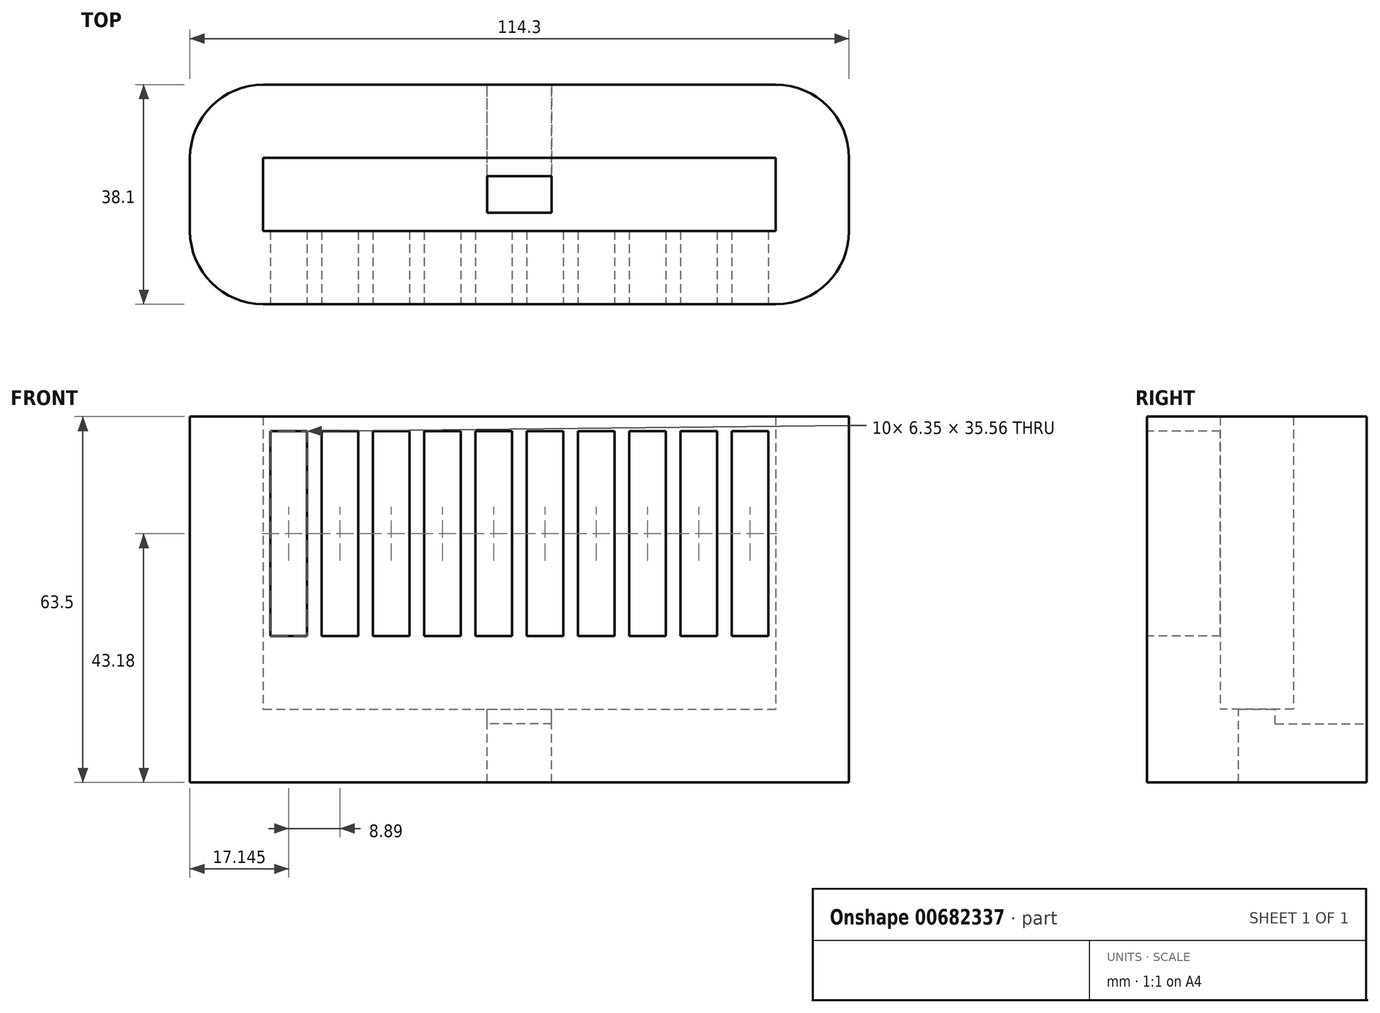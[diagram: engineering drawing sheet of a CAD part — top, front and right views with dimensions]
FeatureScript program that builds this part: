
annotation { "Feature Type Name" : "Feature", "Feature Type Description" : "" }
export const myFeature = defineFeature(function(context is Context, id is Id, definition is map)
    precondition{}
    {
        {
            var Q0;
            Q0=qCreatedBy(makeId("Top.planeOp"),FACE);
            var sketch = newSketch(context, id + "F0", { "sketchPlane" : qUnion([Q0])});
            skLineSegment(sketch, "E0.bottom", {"start": v(0, 0) * mm, "end": v(114.3, 0) * mm});
            skLineSegment(sketch, "E0.top", {"start": v(0, -38.1) * mm, "end": v(114.3, -38.1) * mm});
            skLineSegment(sketch, "E0.left", {"start": v(0, 0) * mm, "end": v(0, -38.1) * mm});
            skLineSegment(sketch, "E0.right", {"start": v(114.3, 0) * mm, "end": v(114.3, -38.1) * mm});
            skLineSegment(sketch, "E1.bottom", {"start": v(12.7, -12.7) * mm, "end": v(101.6, -12.7) * mm});
            skLineSegment(sketch, "E1.top", {"start": v(12.7, -25.4) * mm, "end": v(101.6, -25.4) * mm});
            skLineSegment(sketch, "E1.left", {"start": v(12.7, -12.7) * mm, "end": v(12.7, -25.4) * mm});
            skLineSegment(sketch, "E1.right", {"start": v(101.6, -12.7) * mm, "end": v(101.6, -25.4) * mm});
            skPoint(sketch, "E2", {"position": v(57.15, -12.7) * mm});
            skPoint(sketch, "E3", {"position": v(57.15, 0) * mm});
            skPoint(sketch, "E4", {"position": v(57.15, -38.1) * mm});
            skPoint(sketch, "E5", {"position": v(57.15, -25.4) * mm});
            skPoint(sketch, "E6", {"position": v(0, -19.05) * mm});
            skPoint(sketch, "E7", {"position": v(12.7, -19.05) * mm});
            skPoint(sketch, "E8", {"position": v(101.6, -19.05) * mm});
            skPoint(sketch, "E9", {"position": v(114.3, -19.05) * mm});
            skLineSegment(sketch, "E10", {"start": v(57.15, -12.7) * mm, "end": v(57.15, 0) * mm, "construction": true});
            skLineSegment(sketch, "E11", {"start": v(101.6, -19.05) * mm, "end": v(114.3, -19.05) * mm, "construction": true});
            skLineSegment(sketch, "E12", {"start": v(57.15, -25.4) * mm, "end": v(57.15, -38.1) * mm, "construction": true});
            skLineSegment(sketch, "E13", {"start": v(12.7, -19.05) * mm, "end": v(0, -19.05) * mm, "construction": true});
            skSolve(sketch);
        }
        {
            var Q0;
            Q0=makeQuery(id+"F0.imprint","IMPRINT",FACE,{"disambiguationData":[TD([[makeQuery(id+"F0.imprint","IMPRINT",EDGE,{"derivedFrom":sQuery(id+"F0.wireOp",EDGE,"E0.bottom")}),-1.0]])]});
            extrude(context, id + "F1", {"entities" : qUnion([Q0]), "depth" : 63.5 * mm, "offsetDistance" : 25.4 * mm});
        }
        {
            var Q0;
            Q0=makeQuery(id+"F0.imprint","IMPRINT",FACE,{"disambiguationData":[TD([[makeQuery(id+"F0.imprint","IMPRINT",EDGE,{"derivedFrom":sQuery(id+"F0.wireOp",EDGE,"E1.bottom")}),-1.0]])]});
            extrude(context, id + "F2", {"entities" : qUnion([Q0]), "operationType" : NewBodyOperationType.ADD, "depth" : 12.7 * mm, "offsetDistance" : 25.4 * mm});
        }
        {
            var Q0;
            Q0=makeQuery(id+"F1.opExtrude","SWEPT_FACE",FACE,{"disambiguationData":[OSD([sQuery(id+"F0.wireOp",EDGE,"E0.top")])]});
            var sketch = newSketch(context, id + "F3", { "sketchPlane" : qUnion([Q0])});
            skLineSegment(sketch, "E14.bottom", {"start": v(13.97, 60.96) * mm, "end": v(20.32, 60.96) * mm});
            skLineSegment(sketch, "E14.top", {"start": v(13.97, 25.4) * mm, "end": v(20.32, 25.4) * mm});
            skLineSegment(sketch, "E14.left", {"start": v(20.32, 60.96) * mm, "end": v(20.32, 25.4) * mm});
            skLineSegment(sketch, "E14.right", {"start": v(13.97, 60.96) * mm, "end": v(13.97, 25.4) * mm});
            skLineSegment(sketch, "E15.1.0.0", {"start": v(29.21, 60.96) * mm, "end": v(29.21, 25.4) * mm});
            skLineSegment(sketch, "E15.1.0.1", {"start": v(22.86, 60.96) * mm, "end": v(29.21, 60.96) * mm});
            skLineSegment(sketch, "E15.1.0.2", {"start": v(22.86, 60.96) * mm, "end": v(22.86, 25.4) * mm});
            skLineSegment(sketch, "E15.1.0.3", {"start": v(22.86, 25.4) * mm, "end": v(29.21, 25.4) * mm});
            skLineSegment(sketch, "E15.2.0.0", {"start": v(38.1, 60.96) * mm, "end": v(38.1, 25.4) * mm});
            skLineSegment(sketch, "E15.2.0.1", {"start": v(31.75, 60.96) * mm, "end": v(38.1, 60.96) * mm});
            skLineSegment(sketch, "E15.2.0.2", {"start": v(31.75, 60.96) * mm, "end": v(31.75, 25.4) * mm});
            skLineSegment(sketch, "E15.2.0.3", {"start": v(31.75, 25.4) * mm, "end": v(38.1, 25.4) * mm});
            skLineSegment(sketch, "E15.3.0.0", {"start": v(47, 60.96) * mm, "end": v(47, 25.4) * mm});
            skLineSegment(sketch, "E15.3.0.1", {"start": v(40.64, 60.96) * mm, "end": v(46.99, 60.96) * mm});
            skLineSegment(sketch, "E15.3.0.2", {"start": v(40.64, 60.96) * mm, "end": v(40.64, 25.4) * mm});
            skLineSegment(sketch, "E15.3.0.3", {"start": v(40.64, 25.4) * mm, "end": v(47, 25.4) * mm});
            skLineSegment(sketch, "E15.4.0.0", {"start": v(55.88, 60.96) * mm, "end": v(55.88, 25.4) * mm});
            skLineSegment(sketch, "E15.4.0.1", {"start": v(49.53, 60.96) * mm, "end": v(55.88, 60.96) * mm});
            skLineSegment(sketch, "E15.4.0.2", {"start": v(49.53, 60.96) * mm, "end": v(49.53, 25.4) * mm});
            skLineSegment(sketch, "E15.4.0.3", {"start": v(49.53, 25.4) * mm, "end": v(55.88, 25.4) * mm});
            skLineSegment(sketch, "E15.5.0.0", {"start": v(64.77, 60.96) * mm, "end": v(64.77, 25.4) * mm});
            skLineSegment(sketch, "E15.5.0.1", {"start": v(58.42, 60.96) * mm, "end": v(64.77, 60.96) * mm});
            skLineSegment(sketch, "E15.5.0.2", {"start": v(58.42, 60.96) * mm, "end": v(58.42, 25.4) * mm});
            skLineSegment(sketch, "E15.5.0.3", {"start": v(58.42, 25.4) * mm, "end": v(64.77, 25.4) * mm});
            skLineSegment(sketch, "E15.6.0.0", {"start": v(73.66, 60.96) * mm, "end": v(73.66, 25.4) * mm});
            skLineSegment(sketch, "E15.6.0.1", {"start": v(67.3, 60.96) * mm, "end": v(73.66, 60.96) * mm});
            skLineSegment(sketch, "E15.6.0.2", {"start": v(67.3, 60.96) * mm, "end": v(67.3, 25.4) * mm});
            skLineSegment(sketch, "E15.6.0.3", {"start": v(67.31, 25.4) * mm, "end": v(73.66, 25.4) * mm});
            skLineSegment(sketch, "E15.7.0.0", {"start": v(82.55, 60.96) * mm, "end": v(82.55, 25.4) * mm});
            skLineSegment(sketch, "E15.7.0.1", {"start": v(76.2, 60.96) * mm, "end": v(82.55, 60.96) * mm});
            skLineSegment(sketch, "E15.7.0.2", {"start": v(76.2, 60.96) * mm, "end": v(76.2, 25.4) * mm});
            skLineSegment(sketch, "E15.7.0.3", {"start": v(76.2, 25.4) * mm, "end": v(82.55, 25.4) * mm});
            skLineSegment(sketch, "E15.8.0.0", {"start": v(91.44, 60.96) * mm, "end": v(91.44, 25.4) * mm});
            skLineSegment(sketch, "E15.8.0.1", {"start": v(85.1, 60.96) * mm, "end": v(91.44, 60.96) * mm});
            skLineSegment(sketch, "E15.8.0.2", {"start": v(85.09, 60.96) * mm, "end": v(85.09, 25.4) * mm});
            skLineSegment(sketch, "E15.8.0.3", {"start": v(85.1, 25.4) * mm, "end": v(91.44, 25.4) * mm});
            skLineSegment(sketch, "E15.9.0.0", {"start": v(100.33, 60.96) * mm, "end": v(100.33, 25.4) * mm});
            skLineSegment(sketch, "E15.9.0.1", {"start": v(93.98, 60.96) * mm, "end": v(100.33, 60.96) * mm});
            skLineSegment(sketch, "E15.9.0.2", {"start": v(93.98, 60.96) * mm, "end": v(93.98, 25.4) * mm});
            skLineSegment(sketch, "E15.9.0.3", {"start": v(93.98, 25.4) * mm, "end": v(100.33, 25.4) * mm});
            skLineSegment(sketch, "E15.direction1", {"start": v(13.97, 25.4) * mm, "end": v(22.86, 25.4) * mm, "construction": true});
            skSolve(sketch);
        }
        {
            var Q0;
            Q0=makeQuery(id+"F3.imprint","IMPRINT",FACE,{"disambiguationData":[TD([[makeQuery(id+"F3.imprint","IMPRINT",EDGE,{"derivedFrom":sQuery(id+"F3.wireOp",EDGE,"E14.bottom")}),-1.0]])]});
            var Q1;
            Q1=makeQuery(id+"F3.imprint","IMPRINT",FACE,{"disambiguationData":[TD([[makeQuery(id+"F3.imprint","IMPRINT",EDGE,{"derivedFrom":sQuery(id+"F3.wireOp",EDGE,"E15.1.0.0")}),-1.0]])]});
            var Q2;
            Q2=makeQuery(id+"F3.imprint","IMPRINT",FACE,{"disambiguationData":[TD([[makeQuery(id+"F3.imprint","IMPRINT",EDGE,{"derivedFrom":sQuery(id+"F3.wireOp",EDGE,"E15.2.0.0")}),-1.0]])]});
            var Q3;
            Q3=makeQuery(id+"F3.imprint","IMPRINT",FACE,{"disambiguationData":[TD([[makeQuery(id+"F3.imprint","IMPRINT",EDGE,{"derivedFrom":sQuery(id+"F3.wireOp",EDGE,"E15.3.0.0")}),-1.0]])]});
            var Q4;
            Q4=makeQuery(id+"F3.imprint","IMPRINT",FACE,{"disambiguationData":[TD([[makeQuery(id+"F3.imprint","IMPRINT",EDGE,{"derivedFrom":sQuery(id+"F3.wireOp",EDGE,"E15.4.0.0")}),-1.0]])]});
            var Q5;
            Q5=makeQuery(id+"F3.imprint","IMPRINT",FACE,{"disambiguationData":[TD([[makeQuery(id+"F3.imprint","IMPRINT",EDGE,{"derivedFrom":sQuery(id+"F3.wireOp",EDGE,"E15.5.0.0")}),-1.0]])]});
            var Q6;
            Q6=makeQuery(id+"F3.imprint","IMPRINT",FACE,{"disambiguationData":[TD([[makeQuery(id+"F3.imprint","IMPRINT",EDGE,{"derivedFrom":sQuery(id+"F3.wireOp",EDGE,"E15.6.0.0")}),-1.0]])]});
            var Q7;
            Q7=makeQuery(id+"F3.imprint","IMPRINT",FACE,{"disambiguationData":[TD([[makeQuery(id+"F3.imprint","IMPRINT",EDGE,{"derivedFrom":sQuery(id+"F3.wireOp",EDGE,"E15.7.0.0")}),-1.0]])]});
            var Q8;
            Q8=makeQuery(id+"F3.imprint","IMPRINT",FACE,{"disambiguationData":[TD([[makeQuery(id+"F3.imprint","IMPRINT",EDGE,{"derivedFrom":sQuery(id+"F3.wireOp",EDGE,"E15.8.0.0")}),-1.0]])]});
            var Q9;
            Q9=makeQuery(id+"F3.imprint","IMPRINT",FACE,{"disambiguationData":[TD([[makeQuery(id+"F3.imprint","IMPRINT",EDGE,{"derivedFrom":sQuery(id+"F3.wireOp",EDGE,"E15.9.0.0")}),-1.0]])]});
            extrude(context, id + "F4", {"entities" : qUnion([Q0, Q1, Q2, Q3, Q4, Q5, Q6, Q7, Q8, Q9]), "operationType" : NewBodyOperationType.REMOVE, "oppositeDirection" : true, "depth" : 15.24 * mm, "offsetDistance" : 25.4 * mm});
        }
        {
            var Q0;
            Q0=makeQuery(id+"F4.boolean.opBoolean","MERGE",FACE,{"derivedFrom":[makeQuery(id+"F2.opExtrude","CAP_FACE",FACE,{"disambiguationData":[OSD([sQuery(id+"F0.wireOp",EDGE,"E1.bottom"),sQuery(id+"F0.wireOp",EDGE,"E1.top"),sQuery(id+"F0.wireOp",EDGE,"E1.left"),sQuery(id+"F0.wireOp",EDGE,"E1.right")])],"isStart":false}),makeQuery(id+"F4.opExtrude","SWEPT_FACE",FACE,{"disambiguationData":[OSD([sQuery(id+"F3.wireOp",EDGE,"E14.top")])]}),makeQuery(id+"F4.opExtrude","SWEPT_FACE",FACE,{"disambiguationData":[OSD([sQuery(id+"F3.wireOp",EDGE,"E15.1.0.3")])]}),makeQuery(id+"F4.opExtrude","SWEPT_FACE",FACE,{"disambiguationData":[OSD([sQuery(id+"F3.wireOp",EDGE,"E15.2.0.3")])]}),makeQuery(id+"F4.opExtrude","SWEPT_FACE",FACE,{"disambiguationData":[OSD([sQuery(id+"F3.wireOp",EDGE,"E15.3.0.3")])]}),makeQuery(id+"F4.opExtrude","SWEPT_FACE",FACE,{"disambiguationData":[OSD([sQuery(id+"F3.wireOp",EDGE,"E15.4.0.3")])]}),makeQuery(id+"F4.opExtrude","SWEPT_FACE",FACE,{"disambiguationData":[OSD([sQuery(id+"F3.wireOp",EDGE,"E15.5.0.3")])]}),makeQuery(id+"F4.opExtrude","SWEPT_FACE",FACE,{"disambiguationData":[OSD([sQuery(id+"F3.wireOp",EDGE,"E15.6.0.3")])]}),makeQuery(id+"F4.opExtrude","SWEPT_FACE",FACE,{"disambiguationData":[OSD([sQuery(id+"F3.wireOp",EDGE,"E15.7.0.3")])]}),makeQuery(id+"F4.opExtrude","SWEPT_FACE",FACE,{"disambiguationData":[OSD([sQuery(id+"F3.wireOp",EDGE,"E15.8.0.3")])]}),makeQuery(id+"F4.opExtrude","SWEPT_FACE",FACE,{"disambiguationData":[OSD([sQuery(id+"F3.wireOp",EDGE,"E15.9.0.3")])]})]});
            var sketch = newSketch(context, id + "F5", { "sketchPlane" : qUnion([Q0])});
            skLineSegment(sketch, "E16", {"start": v(51.56, -15.88) * mm, "end": v(62.74, -15.88) * mm});
            skLineSegment(sketch, "E17", {"start": v(62.74, -15.88) * mm, "end": v(62.74, -22.23) * mm});
            skLineSegment(sketch, "E18", {"start": v(62.74, -22.23) * mm, "end": v(51.56, -22.23) * mm});
            skLineSegment(sketch, "E19", {"start": v(51.56, -22.23) * mm, "end": v(51.56, -15.88) * mm});
            skPoint(sketch, "E20", {"position": v(57.15, -15.88) * mm});
            skPoint(sketch, "E21", {"position": v(51.56, -19.05) * mm});
            skSolve(sketch);
        }
        {
            var Q0;
            Q0=makeQuery(id+"F5.imprint","IMPRINT",FACE,{"disambiguationData":[TD([[makeQuery(id+"F5.imprint","IMPRINT",EDGE,{"derivedFrom":sQuery(id+"F5.wireOp",EDGE,"E16")}),-1.0]])]});
            extrude(context, id + "F6", {"entities" : qUnion([Q0]), "operationType" : NewBodyOperationType.REMOVE, "endBound" : BoundingType.THROUGH_ALL, "oppositeDirection" : true, "depth" : 25.4 * mm, "offsetDistance" : 25.4 * mm});
        }
        {
            var Q0;
            Q0=makeQuery(id+"F1.opExtrude","SWEPT_FACE",FACE,{"disambiguationData":[OSD([sQuery(id+"F0.wireOp",EDGE,"E0.bottom")])]});
            var sketch = newSketch(context, id + "F7", { "sketchPlane" : qUnion([Q0])});
            skLineSegment(sketch, "E22.bottom", {"start": v(-62.74, 0) * mm, "end": v(-51.56, 0) * mm});
            skLineSegment(sketch, "E22.top", {"start": v(-62.74, 10.16) * mm, "end": v(-51.56, 10.16) * mm});
            skLineSegment(sketch, "E22.left", {"start": v(-62.74, 0) * mm, "end": v(-62.74, 10.16) * mm});
            skLineSegment(sketch, "E22.right", {"start": v(-51.56, 0) * mm, "end": v(-51.56, 10.16) * mm});
            skSolve(sketch);
        }
        {
            var Q0;
            Q0=makeQuery(id+"F7.imprint","IMPRINT",FACE,{"disambiguationData":[TD([[makeQuery(id+"F7.imprint","IMPRINT",EDGE,{"derivedFrom":sQuery(id+"F7.wireOp",EDGE,"E22.bottom")}),-1.0]])]});
            extrude(context, id + "F8", {"entities" : qUnion([Q0]), "operationType" : NewBodyOperationType.REMOVE, "oppositeDirection" : true, "depth" : 18.29 * mm, "offsetDistance" : 25.4 * mm});
        }
        {
            var Q0;
            Q0=makeQuery(id+"F1.opExtrude","SWEPT_EDGE",EDGE,{"disambiguationData":[OSD([sQuery(id+"F0.wireOp",EDGE,"E0.top"),sQuery(id+"F0.wireOp",EDGE,"E0.left")])]});
            var Q1;
            Q1=makeQuery(id+"F1.opExtrude","SWEPT_EDGE",EDGE,{"disambiguationData":[OSD([sQuery(id+"F0.wireOp",EDGE,"E0.bottom"),sQuery(id+"F0.wireOp",EDGE,"E0.left")])]});
            var Q2;
            Q2=makeQuery(id+"F1.opExtrude","SWEPT_EDGE",EDGE,{"disambiguationData":[OSD([sQuery(id+"F0.wireOp",EDGE,"E0.top"),sQuery(id+"F0.wireOp",EDGE,"E0.right")])]});
            var Q3;
            Q3=makeQuery(id+"F1.opExtrude","SWEPT_EDGE",EDGE,{"disambiguationData":[OSD([sQuery(id+"F0.wireOp",EDGE,"E0.bottom"),sQuery(id+"F0.wireOp",EDGE,"E0.right")])]});
            fillet(context, id + "F9", {"entities" : qUnion([Q0, Q1, Q2, Q3]), "radius" : 12.7 * mm, "tangentPropagation" : true, "allowEdgeOverflow" : false});
        }
    });
